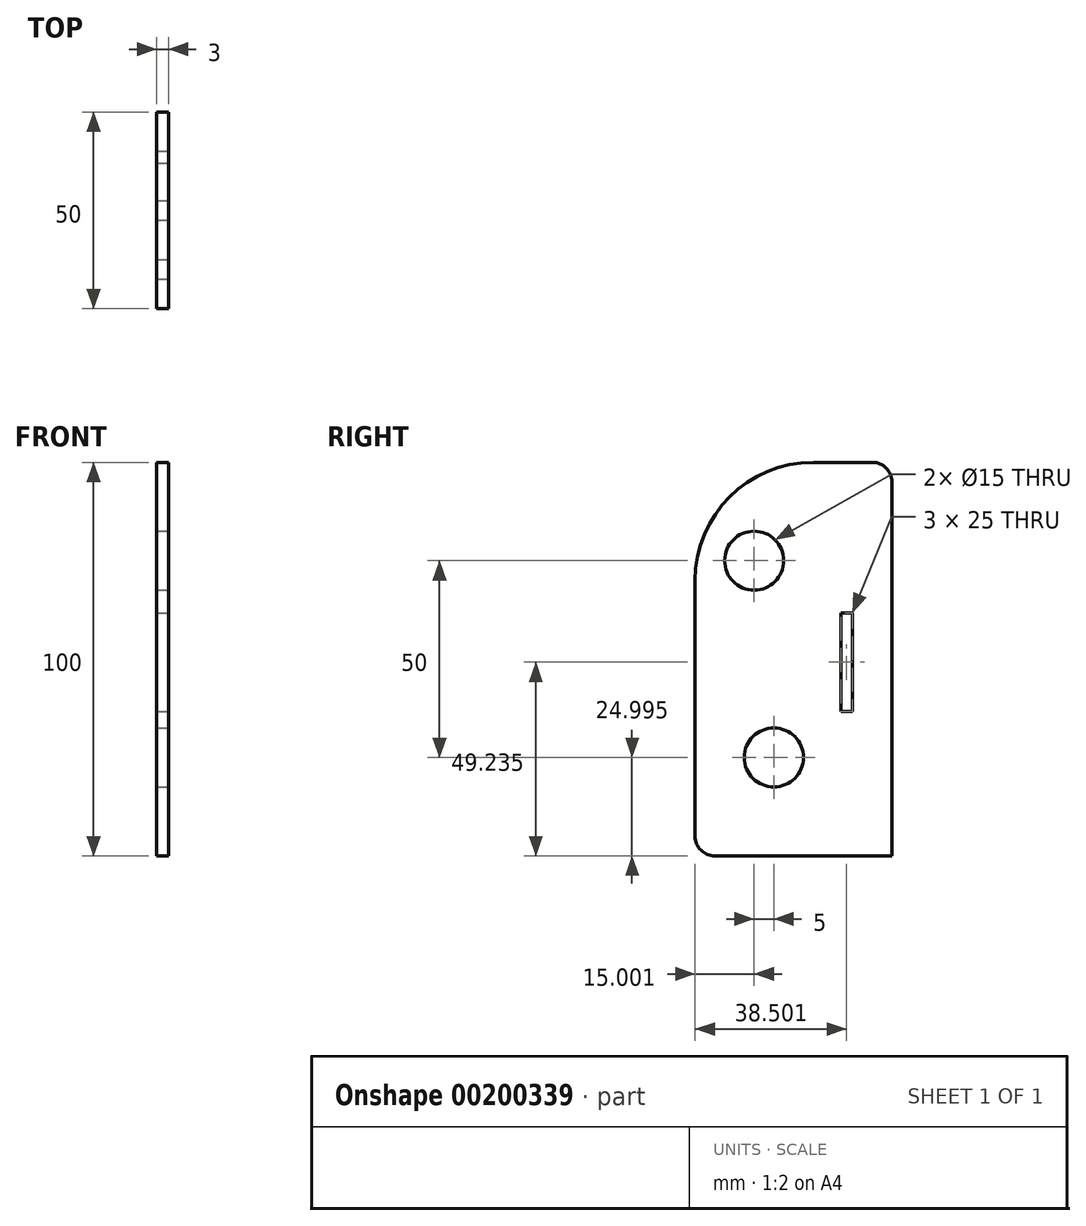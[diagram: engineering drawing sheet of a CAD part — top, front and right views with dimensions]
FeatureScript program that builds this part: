
annotation { "Feature Type Name" : "Feature", "Feature Type Description" : "" }
export const myFeature = defineFeature(function(context is Context, id is Id, definition is map)
    precondition{}
    {
        {
            var Q0;
            Q0=qCreatedBy(makeId("Right.planeOp"),FACE);
            var sketch = newSketch(context, id + "F0", { "sketchPlane" : qUnion([Q0])});
            skLineSegment(sketch, "E0.bottom", {"start": v(-128.74, 120.99) * mm, "end": v(-78.74, 120.99) * mm});
            skLineSegment(sketch, "E0.top", {"start": v(-128.74, 20.99) * mm, "end": v(-78.74, 20.99) * mm});
            skLineSegment(sketch, "E0.left", {"start": v(-128.74, 120.99) * mm, "end": v(-128.74, 20.99) * mm});
            skLineSegment(sketch, "E0.right", {"start": v(-78.74, 120.99) * mm, "end": v(-78.74, 20.99) * mm});
            skSolve(sketch);
        }
        {
            var Q0;
            Q0=makeQuery(id+"F0.imprint","IMPRINT",FACE,{"disambiguationData":[TD([[makeQuery(id+"F0.imprint","IMPRINT",EDGE,{"derivedFrom":sQuery(id+"F0.wireOp",EDGE,"E0.bottom")}),-1.0]])]});
            extrude(context, id + "F1", {"entities" : qUnion([Q0]), "depth" : 3 * mm});
        }
        {
            var Q0;
            Q0=makeQuery(id+"F1.opExtrude","CAP_FACE",FACE,{"disambiguationData":[OSD([sQuery(id+"F0.wireOp",EDGE,"E0.bottom"),sQuery(id+"F0.wireOp",EDGE,"E0.top"),sQuery(id+"F0.wireOp",EDGE,"E0.left"),sQuery(id+"F0.wireOp",EDGE,"E0.right")])],"isStart":false});
            var sketch = newSketch(context, id + "F2", { "sketchPlane" : qUnion([Q0])});
            skLineSegment(sketch, "E1.bottom", {"start": v(-91.74, 82.72) * mm, "end": v(-88.74, 82.72) * mm});
            skLineSegment(sketch, "E1.top", {"start": v(-91.74, 57.72) * mm, "end": v(-88.74, 57.72) * mm});
            skLineSegment(sketch, "E1.left", {"start": v(-91.74, 82.72) * mm, "end": v(-91.74, 57.72) * mm});
            skLineSegment(sketch, "E1.right", {"start": v(-88.74, 82.72) * mm, "end": v(-88.74, 57.72) * mm});
            skSolve(sketch);
        }
        {
            var Q0;
            Q0 = qSketchRegion(id + "F2", true);
            extrude(context, id + "F3", {"entities" : qUnion([Q0]), "operationType" : NewBodyOperationType.REMOVE, "oppositeDirection" : true, "depth" : 3 * mm});
        }
        {
            var Q0;
            Q0=makeQuery(id+"F1.opExtrude","SWEPT_EDGE",EDGE,{"disambiguationData":[OSD([sQuery(id+"F0.wireOp",EDGE,"E0.bottom"),sQuery(id+"F0.wireOp",EDGE,"E0.left")])]});
            fillet(context, id + "F4", {"entities" : qUnion([Q0]), "radius" : 30 * mm, "tangentPropagation" : true, "allowEdgeOverflow" : false});
        }
        {
            var Q0;
            Q0=makeQuery(id+"F1.opExtrude","SWEPT_EDGE",EDGE,{"disambiguationData":[OSD([sQuery(id+"F0.wireOp",EDGE,"E0.bottom"),sQuery(id+"F0.wireOp",EDGE,"E0.right")])]});
            fillet(context, id + "F5", {"entities" : qUnion([Q0]), "radius" : 5 * mm, "tangentPropagation" : true, "allowEdgeOverflow" : false});
        }
        {
            var Q0;
            Q0=makeQuery(id+"F1.opExtrude","SWEPT_EDGE",EDGE,{"disambiguationData":[OSD([sQuery(id+"F0.wireOp",EDGE,"E0.top"),sQuery(id+"F0.wireOp",EDGE,"E0.left")])]});
            fillet(context, id + "F6", {"entities" : qUnion([Q0]), "radius" : 5 * mm, "tangentPropagation" : true, "allowEdgeOverflow" : false});
        }
        {
            var Q0;
            Q0=makeQuery(id+"F1.opExtrude","CAP_FACE",FACE,{"disambiguationData":[OSD([sQuery(id+"F0.wireOp",EDGE,"E0.bottom"),sQuery(id+"F0.wireOp",EDGE,"E0.top"),sQuery(id+"F0.wireOp",EDGE,"E0.left"),sQuery(id+"F0.wireOp",EDGE,"E0.right")])],"isStart":false});
            var sketch = newSketch(context, id + "F7", { "sketchPlane" : qUnion([Q0])});
            skCircle(sketch, "E2", {"center": v(-113.74, 95.99) * mm, "radius": 7.5 * mm});
            skSolve(sketch);
        }
        {
            var Q0;
            Q0 = qSketchRegion(id + "F7", true);
            extrude(context, id + "F8", {"entities" : qUnion([Q0]), "operationType" : NewBodyOperationType.REMOVE, "oppositeDirection" : true, "depth" : 3 * mm});
        }
        {
            var Q0;
            Q0=makeQuery(id+"F1.opExtrude","CAP_FACE",FACE,{"disambiguationData":[OSD([sQuery(id+"F0.wireOp",EDGE,"E0.bottom"),sQuery(id+"F0.wireOp",EDGE,"E0.top"),sQuery(id+"F0.wireOp",EDGE,"E0.left"),sQuery(id+"F0.wireOp",EDGE,"E0.right")])],"isStart":false});
            var sketch = newSketch(context, id + "F9", { "sketchPlane" : qUnion([Q0])});
            skCircle(sketch, "E3", {"center": v(-108.74, 45.99) * mm, "radius": 7.5 * mm});
            skSolve(sketch);
        }
        {
            var Q0;
            Q0 = qSketchRegion(id + "F9", true);
            extrude(context, id + "F10", {"entities" : qUnion([Q0]), "operationType" : NewBodyOperationType.REMOVE, "oppositeDirection" : true, "offsetDistance" : 25 * mm, "depth" : 25 * mm});
        }
    });
